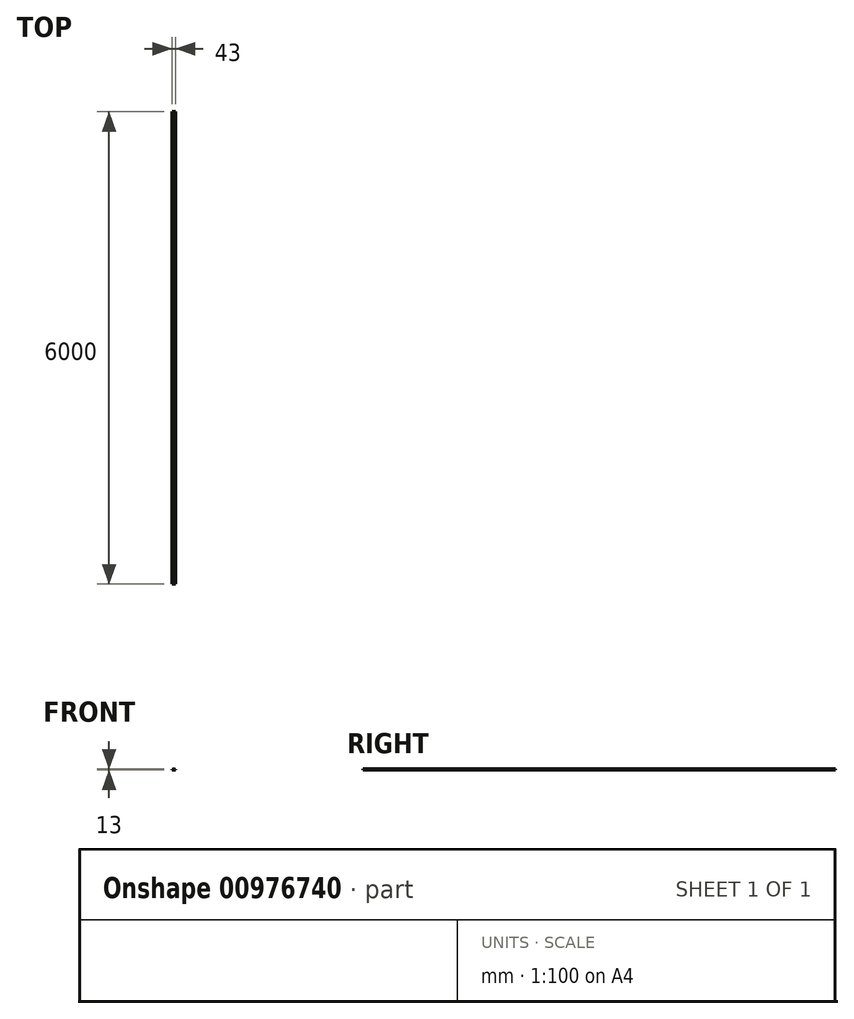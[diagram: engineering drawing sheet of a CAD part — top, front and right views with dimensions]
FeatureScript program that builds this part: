
annotation { "Feature Type Name" : "Feature", "Feature Type Description" : "" }
export const myFeature = defineFeature(function(context is Context, id is Id, definition is map)
    precondition{}
    {
        {
            var Q0;
            Q0=qCreatedBy(makeId("Front.planeOp"),FACE);
            var sketch = newSketch(context, id + "F0", { "sketchPlane" : qUnion([Q0])});
            skLineSegment(sketch, "E0.bottom", {"start": v(-21.5, 0) * mm, "end": v(-15, 0) * mm});
            skLineSegment(sketch, "E0.top", {"start": v(-21.5, 10) * mm, "end": v(-1.5, 10) * mm});
            skLineSegment(sketch, "E0.left", {"start": v(-21.5, 0) * mm, "end": v(-21.5, 10) * mm});
            skLineSegment(sketch, "E0.right", {"start": v(21.5, 0) * mm, "end": v(21.5, 10) * mm});
            skLineSegment(sketch, "E1.top", {"start": v(-15, 6) * mm, "end": v(15, 6) * mm});
            skLineSegment(sketch, "E1.left", {"start": v(-15, 2.6) * mm, "end": v(-15, 6) * mm});
            skLineSegment(sketch, "E1.right", {"start": v(15, 2.6) * mm, "end": v(15, 6) * mm});
            skLineSegment(sketch, "E2.top", {"start": v(-1.5, 13) * mm, "end": v(1.5, 13) * mm});
            skLineSegment(sketch, "E2.left", {"start": v(-1.5, 10) * mm, "end": v(-1.5, 13) * mm});
            skLineSegment(sketch, "E2.right", {"start": v(1.5, 10) * mm, "end": v(1.5, 13) * mm});
            skLineSegment(sketch, "E3", {"start": v(-15, 2.6) * mm, "end": v(-12.4, 2.6) * mm});
            skLineSegment(sketch, "E4", {"start": v(-15, 0) * mm, "end": v(-12.4, 2.6) * mm});
            skLineSegment(sketch, "E5", {"start": v(12.4, 2.6) * mm, "end": v(15, 0) * mm});
            skLineSegment(sketch, "E6.trimOffspring", {"start": v(15, 0) * mm, "end": v(21.5, 0) * mm});
            skLineSegment(sketch, "E7.trimOffspring", {"start": v(12.4, 2.6) * mm, "end": v(15, 2.6) * mm});
            skLineSegment(sketch, "E8.trimOffspring", {"start": v(1.5, 10) * mm, "end": v(21.5, 10) * mm});
            skSolve(sketch);
        }
        {
            var Q0;
            Q0 = qSketchRegion(id + "F0", true);
            extrude(context, id + "F1", {"entities" : qUnion([Q0]), "depth" : 6000 * mm, "offsetDistance" : 25.4 * mm});
        }
    });
